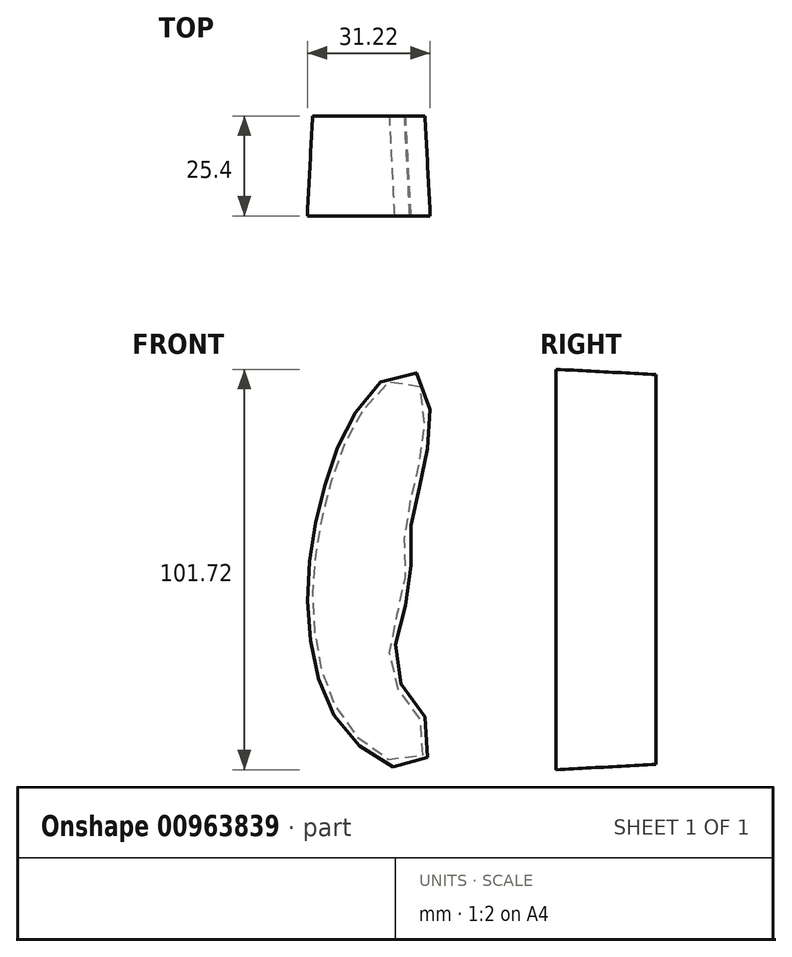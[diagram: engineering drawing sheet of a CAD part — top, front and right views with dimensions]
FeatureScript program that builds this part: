
annotation { "Feature Type Name" : "Feature", "Feature Type Description" : "" }
export const myFeature = defineFeature(function(context is Context, id is Id, definition is map)
    precondition{}
    {
        {
            var Q0;
            Q0=qCreatedBy(makeId("Front.planeOp"),FACE);
            var sketch = newSketch(context, id + "F0", { "sketchPlane" : qUnion([Q0])});
            skFitSpline(sketch, "E0", {"points": [v(4.8, 43.77) * mm, v(-6.52, 35.55) * mm, v(-16.6, 11.06) * mm, v(-19.7, -17.15) * mm, v(-10.55, -45.83) * mm, v(4.18, -55.13) * mm, v(8.2, -52.8) * mm, v(7.12, -42.73) * mm, v(1.7, -35.76) * mm, v(0, -24.44) * mm, v(3.71, -8.63) * mm, v(3.71, 4.24) * mm, v(8.67, 30.28) * mm, v(4.8, 43.77) * mm]});
            skSolve(sketch);
        }
        {
            var Q0;
            Q0=makeQuery(id+"F0.imprint","IMPRINT",FACE,{"disambiguationData":[TD([[makeQuery(id+"F0.imprint","IMPRINT",EDGE,{"derivedFrom":sQuery(id+"F0.wireOp",EDGE,"E0")}),1.0]])]});
            extrude(context, id + "F1", {"entities" : qUnion([Q0]), "depth" : 25.4 * mm, "offsetDistance" : 25.4 * mm, "hasDraft" : true, "draftAngle" : 3 * degree});
        }
    });
